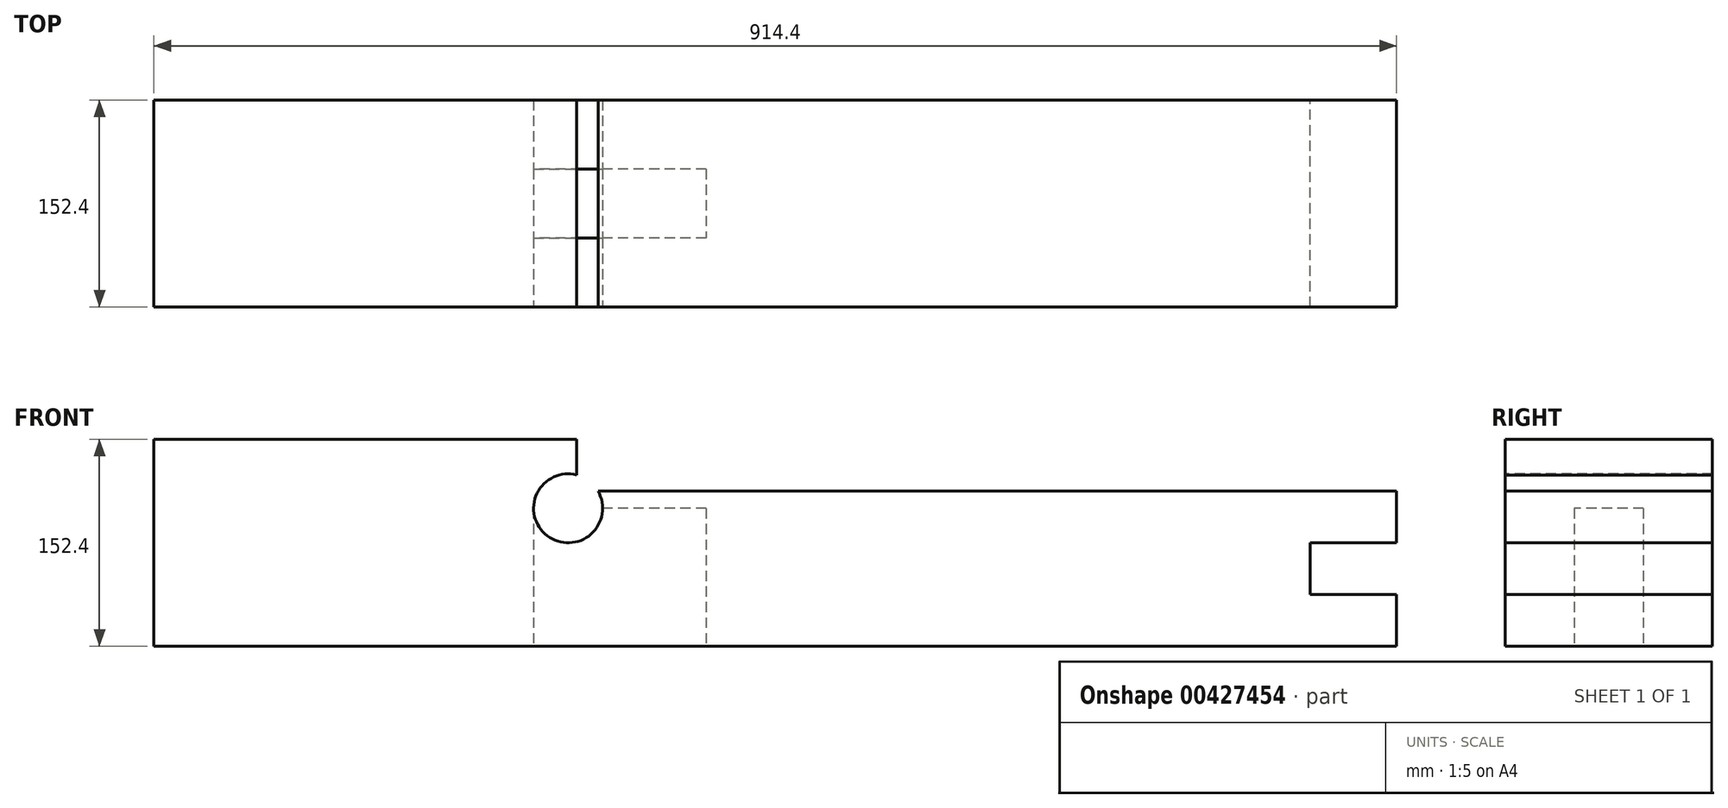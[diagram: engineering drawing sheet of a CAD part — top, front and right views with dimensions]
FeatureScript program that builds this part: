
annotation { "Feature Type Name" : "Feature", "Feature Type Description" : "" }
export const myFeature = defineFeature(function(context is Context, id is Id, definition is map)
    precondition{}
    {
        {
            var Q0;
            Q0=qCreatedBy(makeId("Front.planeOp"),FACE);
            var sketch = newSketch(context, id + "F0", { "sketchPlane" : qUnion([Q0])});
            skLineSegment(sketch, "E0.bottom", {"start": v(-457.2, 76.2) * mm, "end": v(457.2, 76.2) * mm});
            skLineSegment(sketch, "E0.top", {"start": v(-457.2, -76.2) * mm, "end": v(457.2, -76.2) * mm});
            skLineSegment(sketch, "E0.left", {"start": v(-457.2, 76.2) * mm, "end": v(-457.2, -76.2) * mm});
            skLineSegment(sketch, "E0.right", {"start": v(457.2, 76.2) * mm, "end": v(457.2, -76.2) * mm});
            skPoint(sketch, "E0.middle", {"position": v(0, 0) * mm});
            skSolve(sketch);
        }
        {
            var Q0;
            Q0=makeQuery(id+"F0.imprint","IMPRINT",FACE,{"disambiguationData":[TD([[makeQuery(id+"F0.imprint","IMPRINT",EDGE,{"derivedFrom":sQuery(id+"F0.wireOp",EDGE,"E0.bottom")}),-1.0]])]});
            extrude(context, id + "F1", {"entities" : qUnion([Q0]), "depth" : 152.4 * mm});
        }
        {
            var Q0;
            Q0=makeQuery(id+"F1.opExtrude","SWEPT_FACE",FACE,{"disambiguationData":[OSD([sQuery(id+"F0.wireOp",EDGE,"E0.top")])]});
            var sketch = newSketch(context, id + "F2", { "sketchPlane" : qUnion([Q0])});
            skLineSegment(sketch, "E1.bottom", {"start": v(-50.8, 50.8) * mm, "end": v(-177.8, 50.8) * mm});
            skLineSegment(sketch, "E1.top", {"start": v(-50.8, 101.6) * mm, "end": v(-177.8, 101.6) * mm});
            skLineSegment(sketch, "E1.left", {"start": v(-50.8, 50.8) * mm, "end": v(-50.8, 101.6) * mm});
            skLineSegment(sketch, "E1.right", {"start": v(-177.8, 50.8) * mm, "end": v(-177.8, 101.6) * mm});
            skPoint(sketch, "E1.middle", {"position": v(-114.3, 76.2) * mm});
            skSolve(sketch);
        }
        {
            var Q0;
            Q0=makeQuery(id+"F2.imprint","IMPRINT",FACE,{"disambiguationData":[TD([[makeQuery(id+"F2.imprint","IMPRINT",EDGE,{"derivedFrom":sQuery(id+"F2.wireOp",EDGE,"E1.bottom")}),-1.0]])]});
            extrude(context, id + "F3", {"entities" : qUnion([Q0]), "operationType" : NewBodyOperationType.REMOVE, "oppositeDirection" : true, "depth" : 101.6 * mm});
        }
        {
            var Q0;
            Q0=makeQuery(id+"F1.opExtrude","CAP_FACE",FACE,{"disambiguationData":[OSD([sQuery(id+"F0.wireOp",EDGE,"E0.bottom"),sQuery(id+"F0.wireOp",EDGE,"E0.top"),sQuery(id+"F0.wireOp",EDGE,"E0.left"),sQuery(id+"F0.wireOp",EDGE,"E0.right")])],"isStart":false});
            var sketch = newSketch(context, id + "F4", { "sketchPlane" : qUnion([Q0])});
            skCircle(sketch, "E2", {"center": v(-152.4, 25.4) * mm, "radius": 25.4 * mm});
            skSolve(sketch);
        }
        {
            var Q0;
            Q0 = qSketchRegion(id + "F4", true);
            extrude(context, id + "F5", {"entities" : qUnion([Q0]), "operationType" : NewBodyOperationType.REMOVE, "oppositeDirection" : true, "depth" : 337.82 * mm});
        }
        {
            var Q0;
            Q0=makeQuery(id+"F1.opExtrude","CAP_FACE",FACE,{"disambiguationData":[OSD([sQuery(id+"F0.wireOp",EDGE,"E0.bottom"),sQuery(id+"F0.wireOp",EDGE,"E0.top"),sQuery(id+"F0.wireOp",EDGE,"E0.left"),sQuery(id+"F0.wireOp",EDGE,"E0.right")])],"isStart":true});
            var sketch = newSketch(context, id + "F6", { "sketchPlane" : qUnion([Q0])});
            skLineSegment(sketch, "E3.bottom", {"start": v(146.05, 38.1) * mm, "end": v(-457.2, 38.1) * mm});
            skLineSegment(sketch, "E3.top", {"start": v(146.05, 76.2) * mm, "end": v(-457.2, 76.2) * mm});
            skLineSegment(sketch, "E3.left", {"start": v(146.05, 38.1) * mm, "end": v(146.05, 76.2) * mm});
            skLineSegment(sketch, "E3.right", {"start": v(-457.2, 38.1) * mm, "end": v(-457.2, 76.2) * mm});
            skSolve(sketch);
        }
        {
            var Q0;
            {var subQ0=sQuery(id+"F6.wireOp",EDGE,"E3.left");var subQ1=sQuery(id+"F6.wireOp",EDGE,"E3.bottom");var subQ2=makeQuery(id+"F6.imprint","INTERSECT",VERTEX,{"derivedFrom":[subQ1,subQ0]});Q0=makeQuery(id+"F6.imprint","IMPRINT",FACE,{"disambiguationData":[TD([[makeQuery(id+"F6.imprint","IMPRINT",EDGE,{"disambiguationData":[TD([[subQ2,-1.0]])],"derivedFrom":subQ1}),-1.0]])]});}
            var Q1;
            {var subQ2=sQuery(id+"F6.wireOp",EDGE,"E3.top");Q1=makeQuery(id+"F6.imprint","IMPRINT",FACE,{"disambiguationData":[TD([[makeQuery(id+"F6.imprint","IMPRINT",EDGE,{"derivedFrom":subQ2}),1.0]])]});}
            extrude(context, id + "F7", {"entities" : qUnion([Q0, Q1]), "operationType" : NewBodyOperationType.REMOVE, "oppositeDirection" : true, "depth" : 274.32 * mm});
        }
        {
            var Q0;
            Q0=makeQuery(id+"F1.opExtrude","SWEPT_FACE",FACE,{"disambiguationData":[OSD([sQuery(id+"F0.wireOp",EDGE,"E0.right")])]});
            var sketch = newSketch(context, id + "F8", { "sketchPlane" : qUnion([Q0])});
            skCircle(sketch, "E4", {"center": v(-76.2, 38.1) * mm, "radius": 12.7 * mm});
            skSolve(sketch);
        }
        {
            var Q0;
            {var subQ0=sQuery(id+"F8.wireOp",EDGE,"E4");var subQ1=makeQuery(id+"F7.boolean.opBoolean","COPY",EDGE,{"derivedFrom":makeQuery(id+"F7.opExtrude","SWEPT_EDGE",EDGE,{"disambiguationData":[OSD([sQuery(id+"F0.wireOp",EDGE,"E0.right"),sQuery(id+"F6.wireOp",EDGE,"E3.bottom"),sQuery(id+"F6.wireOp",EDGE,"E3.right")])]})});var subQ2=makeQuery(id+"F8.imprint","INTERSECT",VERTEX,{"disambiguationData":[OD(0.0)],"derivedFrom":[subQ1,subQ0]});Q0=makeQuery(id+"F8.imprint","IMPRINT",FACE,{"disambiguationData":[TD([[makeQuery(id+"F8.imprint","IMPRINT",EDGE,{"disambiguationData":[TD([[subQ2,1.0]])],"derivedFrom":subQ0}),1.0]])]});}
            extrude(context, id + "F9", {"entities" : qUnion([Q0]), "operationType" : NewBodyOperationType.REMOVE, "oppositeDirection" : true, "depth" : 492.76 * mm});
        }
        {
            var Q0;
            Q0=makeQuery(id+"F1.opExtrude","SWEPT_FACE",FACE,{"disambiguationData":[OSD([sQuery(id+"F0.wireOp",EDGE,"E0.right")])]});
            var sketch = newSketch(context, id + "F10", { "sketchPlane" : qUnion([Q0])});
            skLineSegment(sketch, "E5.bottom", {"start": v(-152.4, 0) * mm, "end": v(0, 0) * mm});
            skLineSegment(sketch, "E5.top", {"start": v(-152.4, -38.1) * mm, "end": v(0, -38.1) * mm});
            skLineSegment(sketch, "E5.left", {"start": v(-152.4, 0) * mm, "end": v(-152.4, -38.1) * mm});
            skLineSegment(sketch, "E5.right", {"start": v(0, 0) * mm, "end": v(0, -38.1) * mm});
            skSolve(sketch);
        }
        {
            var Q0;
            Q0=makeQuery(id+"F10.imprint","IMPRINT",FACE,{"disambiguationData":[TD([[makeQuery(id+"F10.imprint","IMPRINT",EDGE,{"derivedFrom":sQuery(id+"F10.wireOp",EDGE,"E5.bottom")}),-1.0]])]});
            extrude(context, id + "F11", {"entities" : qUnion([Q0]), "operationType" : NewBodyOperationType.REMOVE, "oppositeDirection" : true, "depth" : 63.5 * mm});
        }
    });
